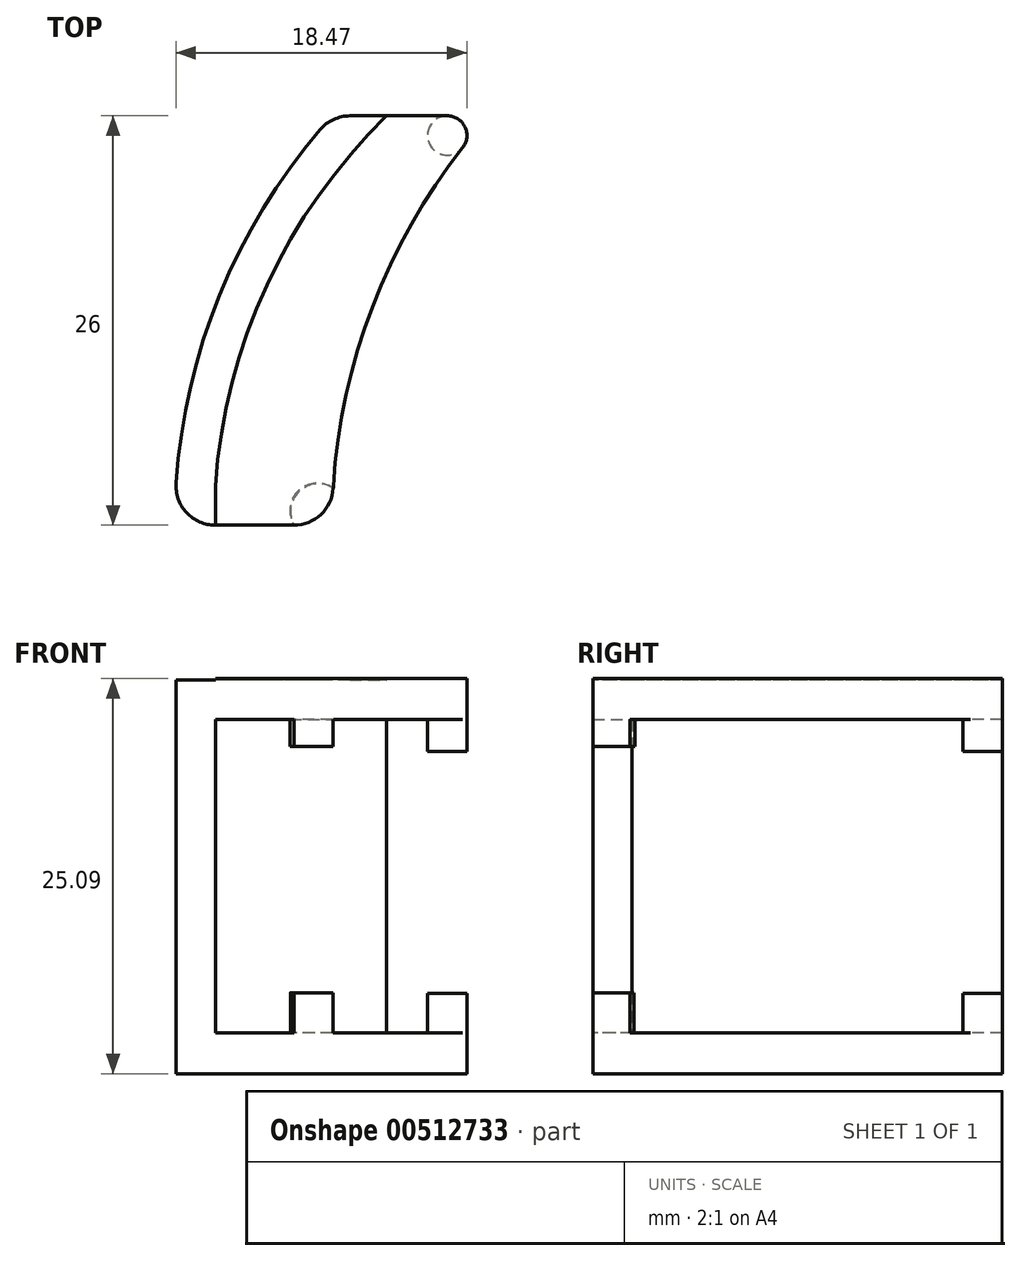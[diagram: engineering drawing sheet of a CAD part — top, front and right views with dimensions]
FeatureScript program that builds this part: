
annotation { "Feature Type Name" : "Feature", "Feature Type Description" : "" }
export const myFeature = defineFeature(function(context is Context, id is Id, definition is map)
    precondition{}
    {
        {
            var Q0;
            Q0=qCreatedBy(makeId("Top.planeOp"),FACE);
            var sketch = newSketch(context, id + "F0", { "sketchPlane" : qUnion([Q0])});
            skLineSegment(sketch, "E0", {"start": v(7.58, 0) * mm, "end": v(2.59, 0) * mm});
            skArc(sketch, "E1", {"start": v(9.23, 25.12) * mm, "mid": v(2.86, 14.63) * mm, "end": v(0.1, 2.67) * mm});
            skLineSegment(sketch, "E2", {"start": v(11.13, 26) * mm, "end": v(17.31, 26) * mm});
            skArc(sketch, "E3", {"start": v(18.3, 23.98) * mm, "mid": v(12.53, 13.8) * mm, "end": v(10.07, 2.35) * mm});
            skPoint(sketch, "E4.visualSharp", {"position": v(10, 0) * mm});
            skArc(sketch, "E4.filletArc", {"start": v(7.58, 0) * mm, "mid": v(9.29, 0.68) * mm, "end": v(10.07, 2.35) * mm});
            skPoint(sketch, "E5.visualSharp", {"position": v(10, 26) * mm});
            skArc(sketch, "E5.filletArc", {"start": v(11.13, 26) * mm, "mid": v(10.08, 25.77) * mm, "end": v(9.23, 25.12) * mm});
            skPoint(sketch, "E6.visualSharp", {"position": v(0, 0) * mm});
            skArc(sketch, "E6.filletArc", {"start": v(0.1, 2.67) * mm, "mid": v(0.76, 0.8) * mm, "end": v(2.59, 0) * mm});
            skPoint(sketch, "E7.visualSharp", {"position": v(20, 26) * mm});
            skArc(sketch, "E7.filletArc", {"start": v(18.3, 23.98) * mm, "mid": v(18.44, 25.3) * mm, "end": v(17.31, 26) * mm});
            skPoint(sketch, "E8.start.orphan", {"position": v(14.22, 26) * mm});
            skPoint(sketch, "E9.start.orphan", {"position": v(5.08, 0) * mm});
            skLineSegment(sketch, "E10", {"start": v(0.2, 4) * mm, "end": v(0.1, 4) * mm});
            skPoint(sketch, "E11.start.orphan", {"position": v(7.65, 6.18) * mm});
            skPoint(sketch, "E12.start.orphan", {"position": v(12.46, 19.52) * mm});
            skPoint(sketch, "E13.orphan", {"position": v(13.8, 21.7) * mm});
            skPoint(sketch, "E14.end.orphan", {"position": v(8.8, 21.7) * mm});
            skPoint(sketch, "E15.end.orphan", {"position": v(2.33, 4) * mm});
            skPoint(sketch, "E16.end.orphan", {"position": v(7.33, 4) * mm});
            skPoint(sketch, "E16.start.orphan", {"position": v(5.08, 4) * mm});
            skSolve(sketch);
        }
        {
            var Q0;
            Q0=makeQuery(id+"F0.imprint","IMPRINT",FACE,{"disambiguationData":[TD([[makeQuery(id+"F0.imprint","IMPRINT",EDGE,{"derivedFrom":sQuery(id+"F0.wireOp",EDGE,"E0")}),-1.0]])]});
            extrude(context, id + "F1", {"entities" : qUnion([Q0]), "depth" : 25 * mm, "offsetDistance" : 25 * mm});
        }
        {
            var Q0;
            Q0=makeQuery(id+"F1.opExtrude","SWEPT_FACE",FACE,{"disambiguationData":[OSD([sQuery(id+"F0.wireOp",EDGE,"E2")])]});
            var Q1;
            Q1=makeQuery(id+"F1.opExtrude","SWEPT_FACE",FACE,{"disambiguationData":[OSD([sQuery(id+"F0.wireOp",EDGE,"E7.filletArc")])]});
            var Q2;
            Q2=makeQuery(id+"F1.opExtrude","SWEPT_FACE",FACE,{"disambiguationData":[OSD([sQuery(id+"F0.wireOp",EDGE,"E3")])]});
            shell(context, id + "F2", {"entities" : qUnion([Q0, Q1, Q2]), "thickness" : 2.5 * mm});
        }
        {
            var Q0;
            Q0=makeQuery(id+"F2.opShell","OFFSET_FACE",FACE,{"disambiguationData":[OSD([sQuery(id+"F0.wireOp",EDGE,"E0")])]});
            extrude(context, id + "F3", {"entities" : qUnion([Q0]), "operationType" : NewBodyOperationType.REMOVE, "oppositeDirection" : true, "depth" : 2.85 * mm, "offsetDistance" : 25 * mm});
        }
        {
            var Q0;
            {var subQ0=sQuery(id+"F0.wireOp",EDGE,"E0");var subQ1=sQuery(id+"F0.wireOp",EDGE,"E7.filletArc");var subQ2=sQuery(id+"F0.wireOp",EDGE,"E6.filletArc");var subQ3=sQuery(id+"F0.wireOp",EDGE,"E5.filletArc");var subQ4=sQuery(id+"F0.wireOp",EDGE,"E4.filletArc");var subQ5=sQuery(id+"F0.wireOp",EDGE,"E3");var subQ6=sQuery(id+"F0.wireOp",EDGE,"E2");var subQ7=sQuery(id+"F0.wireOp",EDGE,"E1");Q0=makeQuery(id+"F3.boolean.opBoolean","MERGE",FACE,{"derivedFrom":[makeQuery(id+"F2.opShell","OFFSET_FACE",FACE,{"disambiguationData":[OSD([subQ0,subQ7,subQ6,subQ5,subQ4,subQ3,subQ2,subQ1]),TDD([makeQuery(id+"F1.opExtrude","CAP_FACE",FACE,{"disambiguationData":[OSD([subQ0,subQ7,subQ6,subQ5,subQ4,subQ3,subQ2,subQ1])],"isStart":true})])]}),makeQuery(id+"F3.opExtrude","SWEPT_FACE",FACE,{"disambiguationData":[OSD([subQ0]),TDD([makeQuery(id+"F2.opShell","OFFSET_EDGE",EDGE,{"disambiguationData":[OSD([subQ0]),TDD([makeQuery(id+"F1.opExtrude","CAP_EDGE",EDGE,{"disambiguationData":[OSD([subQ0])],"isStart":true})])]})])]})]});}
            var sketch = newSketch(context, id + "F4", { "sketchPlane" : qUnion([Q0])});
            skArc(sketch, "E17", {"start": v(17.31, 26) * mm, "mid": v(16.19, 24.2) * mm, "end": v(18.3, 23.98) * mm});
            skSolve(sketch);
        }
        {
            var Q0;
            Q0 = qSketchRegion(id + "F4", true);
            var Q1;
            Q1=makeQuery(id+"F4.imprint","IMPRINT",FACE,{"disambiguationData":[TD([[makeQuery(id+"F4.imprint","IMPRINT",EDGE,{"derivedFrom":sQuery(id+"F4.wireOp",EDGE,"E17")}),1.0]])]});
            var Q2;
            {var subQ0=sQuery(id+"F0.wireOp",EDGE,"E0");var subQ1=sQuery(id+"F0.wireOp",EDGE,"E7.filletArc");var subQ2=sQuery(id+"F0.wireOp",EDGE,"E6.filletArc");var subQ3=sQuery(id+"F0.wireOp",EDGE,"E5.filletArc");var subQ4=sQuery(id+"F0.wireOp",EDGE,"E4.filletArc");var subQ5=sQuery(id+"F0.wireOp",EDGE,"E3");var subQ6=sQuery(id+"F0.wireOp",EDGE,"E2");var subQ7=sQuery(id+"F0.wireOp",EDGE,"E1");Q2=makeQuery(id+"F3.boolean.opBoolean","MERGE",FACE,{"derivedFrom":[makeQuery(id+"F2.opShell","OFFSET_FACE",FACE,{"disambiguationData":[OSD([subQ0,subQ7,subQ6,subQ5,subQ4,subQ3,subQ2,subQ1]),TDD([makeQuery(id+"F1.opExtrude","CAP_FACE",FACE,{"disambiguationData":[OSD([subQ0,subQ7,subQ6,subQ5,subQ4,subQ3,subQ2,subQ1])],"isStart":false})])]}),makeQuery(id+"F3.opExtrude","SWEPT_FACE",FACE,{"disambiguationData":[OSD([subQ0]),TDD([makeQuery(id+"F2.opShell","OFFSET_EDGE",EDGE,{"disambiguationData":[OSD([subQ0]),TDD([makeQuery(id+"F1.opExtrude","CAP_EDGE",EDGE,{"disambiguationData":[OSD([subQ0])],"isStart":false})])]})])]})]});}
            var Q3;
            Q3=makeQuery(id+"F1.opExtrude","CAP_FACE",FACE,{"disambiguationData":[OSD([sQuery(id+"F0.wireOp",EDGE,"E0"),sQuery(id+"F0.wireOp",EDGE,"E1"),sQuery(id+"F0.wireOp",EDGE,"E2"),sQuery(id+"F0.wireOp",EDGE,"E3"),sQuery(id+"F0.wireOp",EDGE,"E4.filletArc"),sQuery(id+"F0.wireOp",EDGE,"E5.filletArc"),sQuery(id+"F0.wireOp",EDGE,"E6.filletArc"),sQuery(id+"F0.wireOp",EDGE,"E7.filletArc")])],"isStart":true});
            extrude(context, id + "F5", {"entities" : qUnion([Q0, Q1, Q2, Q3]), "operationType" : NewBodyOperationType.ADD, "depth" : 2.59 * mm, "offsetDistance" : 25 * mm});
        }
        {
            var Q0;
            {var subQ0=sQuery(id+"F0.wireOp",EDGE,"E0");var subQ1=sQuery(id+"F0.wireOp",EDGE,"E7.filletArc");var subQ2=sQuery(id+"F0.wireOp",EDGE,"E6.filletArc");var subQ3=sQuery(id+"F0.wireOp",EDGE,"E5.filletArc");var subQ4=sQuery(id+"F0.wireOp",EDGE,"E4.filletArc");var subQ5=sQuery(id+"F0.wireOp",EDGE,"E3");var subQ6=sQuery(id+"F0.wireOp",EDGE,"E2");var subQ7=sQuery(id+"F0.wireOp",EDGE,"E1");Q0=makeQuery(id+"F3.boolean.opBoolean","MERGE",FACE,{"derivedFrom":[makeQuery(id+"F2.opShell","OFFSET_FACE",FACE,{"disambiguationData":[OSD([subQ0,subQ7,subQ6,subQ5,subQ4,subQ3,subQ2,subQ1]),TDD([makeQuery(id+"F1.opExtrude","CAP_FACE",FACE,{"disambiguationData":[OSD([subQ0,subQ7,subQ6,subQ5,subQ4,subQ3,subQ2,subQ1])],"isStart":false})])]}),makeQuery(id+"F3.opExtrude","SWEPT_FACE",FACE,{"disambiguationData":[OSD([subQ0]),TDD([makeQuery(id+"F2.opShell","OFFSET_EDGE",EDGE,{"disambiguationData":[OSD([subQ0]),TDD([makeQuery(id+"F1.opExtrude","CAP_EDGE",EDGE,{"disambiguationData":[OSD([subQ0])],"isStart":false})])]})])]})]});}
            var sketch = newSketch(context, id + "F6", { "sketchPlane" : qUnion([Q0])});
            skArc(sketch, "E18", {"start": v(18.3, -23.98) * mm, "mid": v(16.19, -24.2) * mm, "end": v(17.31, -26) * mm});
            skSolve(sketch);
        }
        {
            var Q0;
            Q0 = qSketchRegion(id + "F6", true);
            var Q1;
            Q1=makeQuery(id+"F6.imprint","IMPRINT",FACE,{"disambiguationData":[TD([[makeQuery(id+"F6.imprint","IMPRINT",EDGE,{"derivedFrom":sQuery(id+"F6.wireOp",EDGE,"E18")}),1.0]])]});
            extrude(context, id + "F7", {"entities" : qUnion([Q0, Q1]), "operationType" : NewBodyOperationType.ADD, "depth" : 2.02 * mm, "offsetDistance" : 25 * mm});
        }
        {
            var Q0;
            {var subQ0=sQuery(id+"F0.wireOp",EDGE,"E0");var subQ1=sQuery(id+"F0.wireOp",EDGE,"E7.filletArc");var subQ2=sQuery(id+"F0.wireOp",EDGE,"E6.filletArc");var subQ3=sQuery(id+"F0.wireOp",EDGE,"E5.filletArc");var subQ4=sQuery(id+"F0.wireOp",EDGE,"E4.filletArc");var subQ5=sQuery(id+"F0.wireOp",EDGE,"E3");var subQ6=sQuery(id+"F0.wireOp",EDGE,"E2");var subQ7=sQuery(id+"F0.wireOp",EDGE,"E1");Q0=makeQuery(id+"F3.boolean.opBoolean","MERGE",FACE,{"derivedFrom":[makeQuery(id+"F2.opShell","OFFSET_FACE",FACE,{"disambiguationData":[OSD([subQ0,subQ7,subQ6,subQ5,subQ4,subQ3,subQ2,subQ1]),TDD([makeQuery(id+"F1.opExtrude","CAP_FACE",FACE,{"disambiguationData":[OSD([subQ0,subQ7,subQ6,subQ5,subQ4,subQ3,subQ2,subQ1])],"isStart":false})])]}),makeQuery(id+"F3.opExtrude","SWEPT_FACE",FACE,{"disambiguationData":[OSD([subQ0]),TDD([makeQuery(id+"F2.opShell","OFFSET_EDGE",EDGE,{"disambiguationData":[OSD([subQ0]),TDD([makeQuery(id+"F1.opExtrude","CAP_EDGE",EDGE,{"disambiguationData":[OSD([subQ0])],"isStart":false})])]})])]})]});}
            var sketch = newSketch(context, id + "F8", { "sketchPlane" : qUnion([Q0])});
            skArc(sketch, "E19", {"start": v(7.58, 0) * mm, "mid": v(7.87, -2.2) * mm, "end": v(10.07, -2.35) * mm});
            skSolve(sketch);
        }
        {
            var Q0;
            Q0 = qSketchRegion(id + "F8", true);
            var Q1;
            Q1=makeQuery(id+"F8.imprint","IMPRINT",FACE,{"disambiguationData":[TD([[makeQuery(id+"F8.imprint","IMPRINT",EDGE,{"derivedFrom":sQuery(id+"F8.wireOp",EDGE,"E19")}),1.0]])]});
            extrude(context, id + "F9", {"entities" : qUnion([Q0, Q1]), "operationType" : NewBodyOperationType.ADD, "depth" : 1.72 * mm, "offsetDistance" : 25 * mm});
        }
        {
            var Q0;
            {var subQ0=sQuery(id+"F0.wireOp",EDGE,"E7.filletArc");var subQ1=sQuery(id+"F0.wireOp",EDGE,"E6.filletArc");var subQ2=sQuery(id+"F0.wireOp",EDGE,"E5.filletArc");var subQ3=sQuery(id+"F0.wireOp",EDGE,"E4.filletArc");var subQ4=sQuery(id+"F0.wireOp",EDGE,"E3");var subQ5=sQuery(id+"F0.wireOp",EDGE,"E2");var subQ6=sQuery(id+"F0.wireOp",EDGE,"E1");var subQ7=sQuery(id+"F0.wireOp",EDGE,"E0");Q0=makeQuery(id+"F5.opExtrude","CAP_FACE",FACE,{"disambiguationData":[OSD([subQ7,subQ6,subQ5,subQ4,subQ3,subQ2,subQ1,subQ0]),TDD([makeQuery(id+"F1.opExtrude","CAP_FACE",FACE,{"disambiguationData":[OSD([subQ7,subQ6,subQ5,subQ4,subQ3,subQ2,subQ1,subQ0])],"isStart":true})])],"isStart":false});}
            var sketch = newSketch(context, id + "F10", { "sketchPlane" : qUnion([Q0])});
            skArc(sketch, "E20", {"start": v(10.07, 2.35) * mm, "mid": v(7.91, 2.14) * mm, "end": v(7.58, 0) * mm});
            skSolve(sketch);
        }
        {
            var Q0;
            Q0 = qSketchRegion(id + "F10", true);
            var Q1;
            Q1=makeQuery(id+"F10.imprint","IMPRINT",FACE,{"disambiguationData":[TD([[makeQuery(id+"F10.imprint","IMPRINT",EDGE,{"derivedFrom":sQuery(id+"F10.wireOp",EDGE,"E20")}),1.0]])]});
            extrude(context, id + "F11", {"entities" : qUnion([Q0, Q1]), "operationType" : NewBodyOperationType.ADD, "depth" : 2.55 * mm, "offsetDistance" : 25 * mm});
        }
    });
